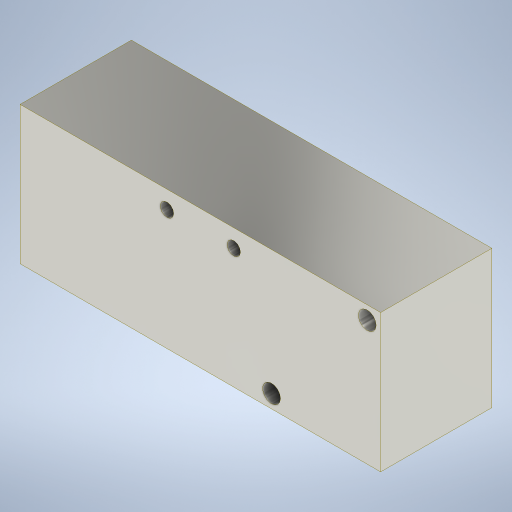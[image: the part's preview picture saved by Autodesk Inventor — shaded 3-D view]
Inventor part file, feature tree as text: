
AUTODESK INVENTOR PART (.ipt)
format: ipt  version: 2023 (Build 270158000, 158)  size: 214,528 bytes
history: native  units: mm
features: extrude x1, sketch x1
ambient origin geometry x8: Origin, YZ Plane, XZ Plane, XY Plane, X Axis, Y Axis, Z Axis, Center Point
bodies: Solid1 (feature_tree)
feature tree (2):
  extrude  "Extrusion1"  Depth=81.0mm
  sketch  "Sketch1"  dims[d0=3.0mm d1=81.0mm d2=31.0mm d3=4.0mm d4=3.0mm d5=24.5mm d6=4.0mm d7=3.0mm d8=30.0mm d9=3.0mm d11=4.0mm d12=15.0mm d13=3.0mm d14=25.0mm d15=0.0mm]
